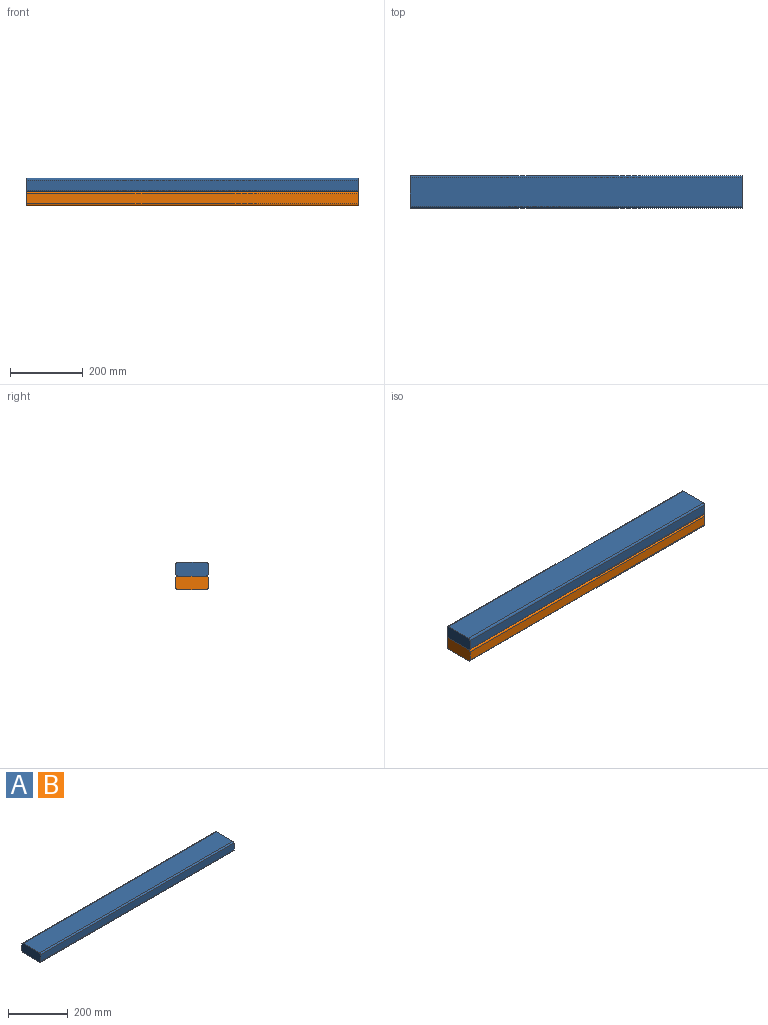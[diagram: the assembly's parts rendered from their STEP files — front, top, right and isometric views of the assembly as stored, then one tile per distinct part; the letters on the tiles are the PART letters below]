
ASSEMBLY  parts=2 mates=1
PART A: 10 faces, bbox 914.4x88.9x38.1 mm
  f0: plane 914.4x78.74mm, normal (0,0,-1), area 71999.9mm2, adj f4,f5,f6,f9
  f1: plane 914.4x27.94mm, normal (0,1,0), area 25548.3mm2, adj f4,f5,f6,f7
  f2: plane 914.4x78.74mm, normal (0,0,1), area 71999.9mm2, adj f4,f5,f7,f8
  f3: plane 914.4x27.94mm, normal (0,-1,0), area 25548.3mm2, adj f4,f5,f8,f9
  f4: plane 88.9x38.1mm, normal (1,0,0), area 3364.9mm2, adj f0,f1,f2,f3,f6,f7,f8,f9
  f5: plane 88.9x38.1mm, normal (-1,0,0), area 3364.9mm2, adj f0,f1,f2,f3,f6,f7,f8,f9
  f6: cylinder r=5.08mm len=914.4mm, axis (1,0,0), area 7296.6mm2, adj f0,f1,f4,f5
  f7: cylinder r=5.08mm len=914.4mm, axis (-1,0,0), area 7296.6mm2, adj f1,f2,f4,f5
  f8: cylinder r=5.08mm len=914.4mm, axis (1,0,0), area 7296.6mm2, adj f2,f3,f4,f5
  f9: cylinder r=5.08mm len=914.4mm, axis (-1,0,0), area 7296.6mm2, adj f0,f3,f4,f5
PART B: same geometry as A
PLACE A t=(-457.2,0,57.15)mm
PLACE B t=(-457.2,0,19.05)mm
MATE fastened B.f2 <-> A.f0  axis (0,0,1) through (0,0,38.1)mm
